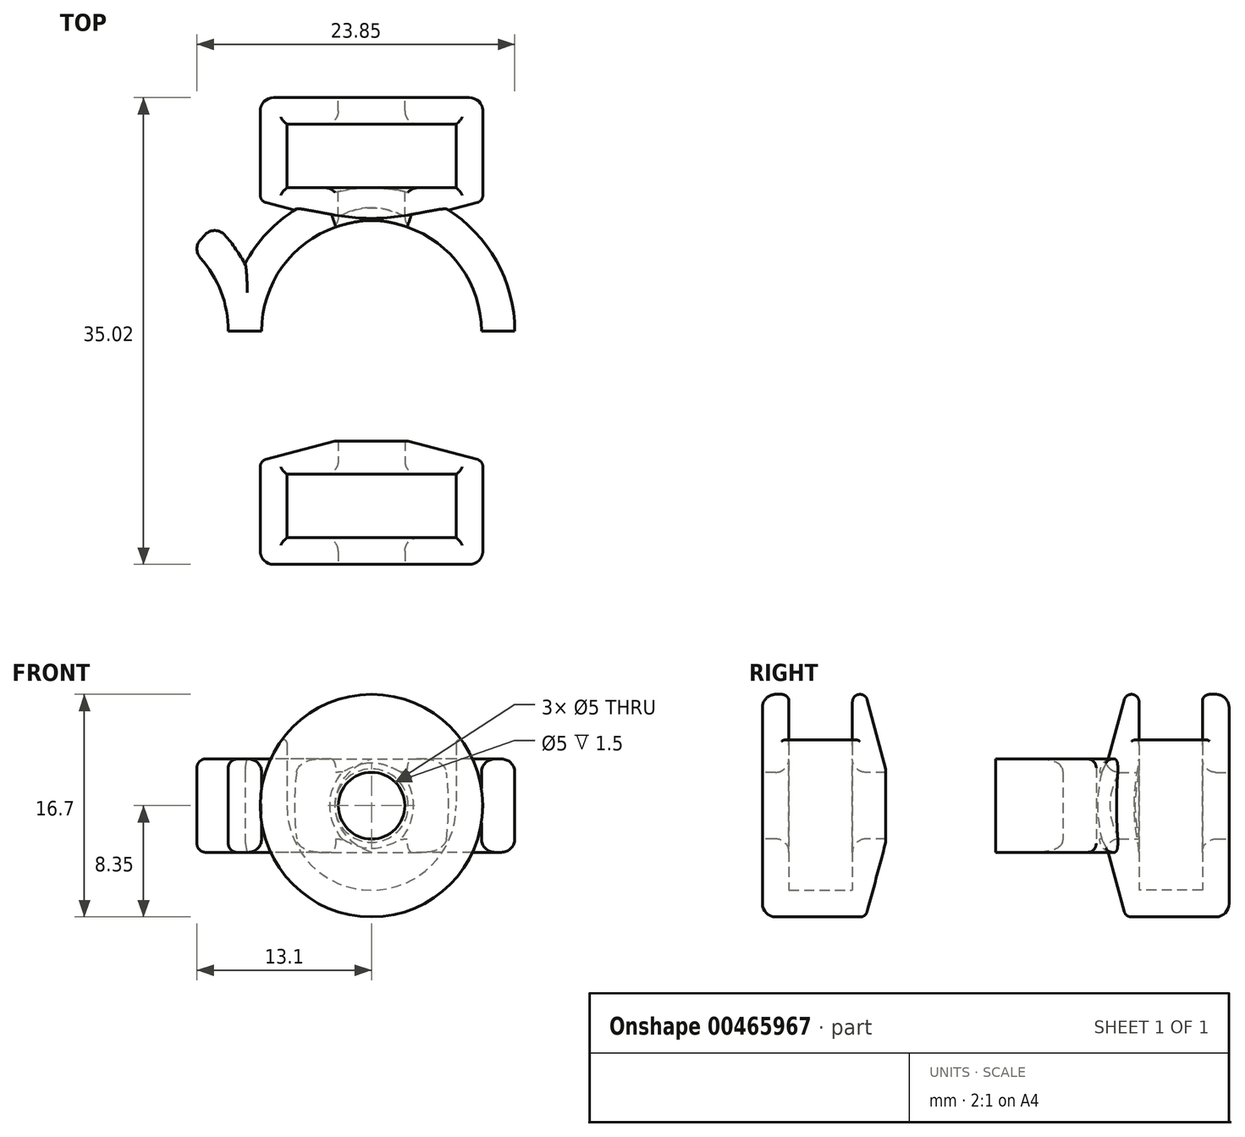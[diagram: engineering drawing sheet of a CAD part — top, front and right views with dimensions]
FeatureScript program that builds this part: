
annotation { "Feature Type Name" : "Feature", "Feature Type Description" : "" }
export const myFeature = defineFeature(function(context is Context, id is Id, definition is map)
    precondition{}
    {
        {
            var Q0;
            Q0=qCreatedBy(makeId("Top.planeOp"),FACE);
            var sketch = newSketch(context, id + "F0", { "sketchPlane" : qUnion([Q0])});
            skCircle(sketch, "E0", {"center": v(0, 0) * mm, "radius": 8.25 * mm});
            skCircle(sketch, "E1", {"center": v(0, 0) * mm, "radius": 10.75 * mm});
            skSolve(sketch);
        }
        {
            var Q0;
            Q0=qCreatedBy(makeId("Top.planeOp"),FACE);
            var sketch = newSketch(context, id + "F1", { "sketchPlane" : qUnion([Q0])});
            skLineSegment(sketch, "E2", {"start": v(0, 0) * mm, "end": v(0, 8.25) * mm, "construction": true});
            skLineSegment(sketch, "E3", {"start": v(0, 8.25) * mm, "end": v(8.35, 8.25) * mm});
            skLineSegment(sketch, "E4", {"start": v(8.35, 8.25) * mm, "end": v(8.35, 17.51) * mm});
            skLineSegment(sketch, "E5", {"start": v(8.35, 17.51) * mm, "end": v(0, 17.51) * mm});
            skLineSegment(sketch, "E6", {"start": v(0, 17.51) * mm, "end": v(0, 15.51) * mm});
            skLineSegment(sketch, "E7", {"start": v(0, 15.51) * mm, "end": v(6.35, 15.51) * mm});
            skLineSegment(sketch, "E8", {"start": v(6.35, 15.51) * mm, "end": v(6.35, 10.75) * mm});
            skLineSegment(sketch, "E9", {"start": v(0, 8.25) * mm, "end": v(0, 10.75) * mm});
            skLineSegment(sketch, "E10", {"start": v(0, 10.75) * mm, "end": v(6.35, 10.75) * mm});
            skLineSegment(sketch, "E11", {"start": v(0, 15.51) * mm, "end": v(0, 10.75) * mm, "construction": true});
            skSolve(sketch);
        }
        {
            var Q0;
            Q0 = qSketchRegion(id + "F1", true);
            var Q1;
            Q1=sQuery(id+"F1.wireOp",EDGE,"E2");
            revolve(context, id + "F2", {"surfaceOperationType" : NewSurfaceOperationType.NEW, "entities" : qUnion([Q0]), "axis" : qUnion([Q1]), "revolveType" : RevolveType.FULL});
        }
        {
            var Q0;
            Q0 = qSketchRegion(id + "F0", true);
            extrude(context, id + "F3", {"entities" : qUnion([Q0]), "endBound" : BoundingType.SYMMETRIC, "depth" : 7 * mm, "offsetDistance" : 25 * mm});
        }
        {
            var Q0;
            Q0=qCreatedBy(makeId("Top.planeOp"),FACE);
            var sketch = newSketch(context, id + "F4", { "sketchPlane" : qUnion([Q0])});
            skLineSegment(sketch, "E12", {"start": v(6.35, 10.75) * mm, "end": v(6.35, 15.51) * mm});
            skLineSegment(sketch, "E13", {"start": v(6.35, 15.51) * mm, "end": v(-6.35, 15.51) * mm});
            skLineSegment(sketch, "E14", {"start": v(-6.35, 15.51) * mm, "end": v(-6.35, 10.75) * mm});
            skLineSegment(sketch, "E15", {"start": v(0, 10.75) * mm, "end": v(-6.35, 10.75) * mm});
            skLineSegment(sketch, "E16", {"start": v(0, 10.75) * mm, "end": v(6.35, 10.75) * mm});
            skLineSegment(sketch, "E17", {"start": v(0, 0) * mm, "end": v(0, 8.25) * mm, "construction": true});
            skLineSegment(sketch, "E18", {"start": v(0, 8.25) * mm, "end": v(0, 10.75) * mm, "construction": true});
            skSolve(sketch);
        }
        {
            var Q0;
            Q0 = qSketchRegion(id + "F4", true);
            extrude(context, id + "F5", {"entities" : qUnion([Q0]), "operationType" : NewBodyOperationType.REMOVE, "depth" : 9.6 * mm, "offsetDistance" : 25 * mm});
        }
        {
            var Q0;
            Q0=makeQuery(id+"F2.opRevolve","SWEPT_FACE",FACE,{"disambiguationData":[OSD([sQuery(id+"F1.wireOp",EDGE,"E5")])]});
            var sketch = newSketch(context, id + "F6", { "sketchPlane" : qUnion([Q0])});
            skCircle(sketch, "E19", {"center": v(0, 0) * mm, "radius": 2.5 * mm});
            skSolve(sketch);
        }
        {
            var Q0;
            Q0 = qSketchRegion(id + "F6", true);
            extrude(context, id + "F7", {"entities" : qUnion([Q0]), "operationType" : NewBodyOperationType.REMOVE, "oppositeDirection" : true, "depth" : 19.1 * mm, "offsetDistance" : 25 * mm});
        }
        {
            var Q0;
            Q0=makeQuery(id+"F2.opRevolve","SWEPT_EDGE",EDGE,{"disambiguationData":[OSD([sQuery(id+"F1.wireOp",EDGE,"E3"),sQuery(id+"F1.wireOp",EDGE,"E4")])]});
            chamfer(context, id + "F8", {"entities" : qUnion([Q0]), "chamferType" : ChamferType.OFFSET_ANGLE, "width" : 1.5 * mm, "oppositeDirection" : true, "angle" : 75 * degree, "tangentPropagation" : true});
        }
        {
            var Q0;
            Q0=makeQuery(id+"F5.boolean.opBoolean","INTERSECT",EDGE,{"derivedFrom":[makeQuery(id+"F2.opRevolve","SWEPT_FACE",FACE,{"disambiguationData":[OSD([sQuery(id+"F1.wireOp",EDGE,"E4")])]}),makeQuery(id+"F5.opExtrude","SWEPT_FACE",FACE,{"disambiguationData":[OSD([sQuery(id+"F4.wireOp",EDGE,"E14")])]})]});
            var Q1;
            Q1=makeQuery(id+"F5.boolean.opBoolean","INTERSECT",EDGE,{"derivedFrom":[makeQuery(id+"F2.opRevolve","SWEPT_FACE",FACE,{"disambiguationData":[OSD([sQuery(id+"F1.wireOp",EDGE,"E4")])]}),makeQuery(id+"F5.opExtrude","SWEPT_FACE",FACE,{"disambiguationData":[OSD([sQuery(id+"F4.wireOp",EDGE,"E12")])]})]});
            fillet(context, id + "F9", {"entities" : qUnion([Q0, Q1]), "radius" : .25 * mm, "tangentPropagation" : true, "allowEdgeOverflow" : false});
        }
        {
            var Q0;
            {var subQ0=sQuery(id+"F1.wireOp",EDGE,"E4");Q0=makeQuery(id+"F8.opChamfer","BLEND_EDGE",EDGE,{"blendedFrom":[makeQuery(id+"F2.opRevolve","SWEPT_EDGE",EDGE,{"disambiguationData":[OSD([sQuery(id+"F1.wireOp",EDGE,"E3"),subQ0])]}),makeQuery(id+"F2.opRevolve","SWEPT_FACE",FACE,{"disambiguationData":[OSD([subQ0])]})],"blendedInto":[makeQuery(id+"F2.opRevolve","SWEPT_FACE",FACE,{"disambiguationData":[OSD([subQ0])]})]});}
            var Q1;
            Q1=makeQuery(id+"F5.boolean.opBoolean","INTERSECT",EDGE,{"derivedFrom":[makeQuery(id+"F2.opRevolve","SWEPT_FACE",FACE,{"disambiguationData":[OSD([sQuery(id+"F1.wireOp",EDGE,"E4")])]}),makeQuery(id+"F5.opExtrude","SWEPT_FACE",FACE,{"disambiguationData":[OSD([sQuery(id+"F4.wireOp",EDGE,"E15"),sQuery(id+"F4.wireOp",EDGE,"E16")])]})]});
            var Q2;
            Q2=makeQuery(id+"F5.boolean.opBoolean","INTERSECT",EDGE,{"derivedFrom":[makeQuery(id+"F2.opRevolve","SWEPT_FACE",FACE,{"disambiguationData":[OSD([sQuery(id+"F1.wireOp",EDGE,"E4")])]}),makeQuery(id+"F5.opExtrude","SWEPT_FACE",FACE,{"disambiguationData":[OSD([sQuery(id+"F4.wireOp",EDGE,"E13")])]})]});
            fillet(context, id + "F10", {"entities" : qUnion([Q0, Q1, Q2]), "radius" : .55 * mm, "tangentPropagation" : true, "allowEdgeOverflow" : false});
        }
        {
            var Q0;
            Q0=makeQuery(id+"F2.opRevolve","SWEPT_EDGE",EDGE,{"disambiguationData":[OSD([sQuery(id+"F1.wireOp",EDGE,"E4"),sQuery(id+"F1.wireOp",EDGE,"E5")])]});
            var Q1;
            Q1=makeQuery(id+"F7.boolean.opBoolean","COPY",EDGE,{"derivedFrom":makeQuery(id+"F7.opExtrude","CAP_EDGE",EDGE,{"disambiguationData":[OSD([sQuery(id+"F6.wireOp",EDGE,"E19")])],"isStart":true})});
            var Q2;
            Q2=makeQuery(id+"F7.boolean.opBoolean","INTERSECT",EDGE,{"derivedFrom":[makeQuery(id+"F5.boolean.opBoolean","MERGE",FACE,{"derivedFrom":[makeQuery(id+"F2.opRevolve","SWEPT_FACE",FACE,{"disambiguationData":[OSD([sQuery(id+"F1.wireOp",EDGE,"E10")])]}),makeQuery(id+"F5.opExtrude","SWEPT_FACE",FACE,{"disambiguationData":[OSD([sQuery(id+"F4.wireOp",EDGE,"E15"),sQuery(id+"F4.wireOp",EDGE,"E16")])]})]}),makeQuery(id+"F7.opExtrude","SWEPT_FACE",FACE,{"disambiguationData":[OSD([sQuery(id+"F6.wireOp",EDGE,"E19")])]})]});
            var Q3;
            Q3=makeQuery(id+"F7.boolean.opBoolean","INTERSECT",EDGE,{"derivedFrom":[makeQuery(id+"F5.boolean.opBoolean","MERGE",FACE,{"derivedFrom":[makeQuery(id+"F2.opRevolve","SWEPT_FACE",FACE,{"disambiguationData":[OSD([sQuery(id+"F1.wireOp",EDGE,"E7")])]}),makeQuery(id+"F5.opExtrude","SWEPT_FACE",FACE,{"disambiguationData":[OSD([sQuery(id+"F4.wireOp",EDGE,"E13")])]})]}),makeQuery(id+"F7.opExtrude","SWEPT_FACE",FACE,{"disambiguationData":[OSD([sQuery(id+"F6.wireOp",EDGE,"E19")])]})]});
            fillet(context, id + "F11", {"entities" : qUnion([Q0, Q1, Q2, Q3]), "radius" : 1 * mm, "tangentPropagation" : true, "allowEdgeOverflow" : false});
        }
        {
            var Q0;
            Q0=qCreatedBy(makeId("Top.planeOp"),FACE);
            var sketch = newSketch(context, id + "F12", { "sketchPlane" : qUnion([Q0])});
            skCircle(sketch, "E20", {"center": v(0, 0) * mm, "radius": 8.25 * mm, "construction": true});
            skCircle(sketch, "E21", {"center": v(0, 0) * mm, "radius": 10.75 * mm, "construction": true});
            skLineSegment(sketch, "E22", {"start": v(0, 0) * mm, "end": v(-5.52, 6.13) * mm, "construction": true});
            skLineSegment(sketch, "E23", {"start": v(-5.52, 6.13) * mm, "end": v(-7.2, 7.99) * mm, "construction": true});
            skLineSegment(sketch, "E24", {"start": v(0, 0) * mm, "end": v(-8.25, 0) * mm, "construction": true});
            skLineSegment(sketch, "E25", {"start": v(-8.25, 0) * mm, "end": v(-10.75, 0) * mm, "construction": true});
            skArc(sketch, "E26", {"start": v(-8.25, 0) * mm, "mid": v(-7.54, 3.36) * mm, "end": v(-5.52, 6.13) * mm});
            skArc(sketch, "E27", {"start": v(-10.75, 0) * mm, "mid": v(-9.82, 4.37) * mm, "end": v(-7.2, 7.99) * mm});
            skLineSegment(sketch, "E28", {"start": v(-7.2, 7.99) * mm, "end": v(-5.52, 6.13) * mm});
            skLineSegment(sketch, "E29", {"start": v(-8.25, 0) * mm, "end": v(-10.75, 0) * mm});
            skLineSegment(sketch, "E30", {"start": v(-9.5, 0) * mm, "end": v(-9.5, 7.58) * mm, "construction": true});
            skArc(sketch, "E31.MirrorCS", {"start": v(-8.25, 0) * mm, "mid": v(-9.18, 4.37) * mm, "end": v(-11.8, 7.99) * mm});
            skLineSegment(sketch, "E32.MirrorCS", {"start": v(-11.8, 7.99) * mm, "end": v(-13.48, 6.13) * mm});
            skArc(sketch, "E33.MirrorCS", {"start": v(-10.75, 0) * mm, "mid": v(-11.46, 3.36) * mm, "end": v(-13.48, 6.13) * mm});
            skLineSegment(sketch, "E34.MirrorCS", {"start": v(-10.75, 0) * mm, "end": v(-8.25, 0) * mm});
            skSolve(sketch);
        }
        {
            var Q0;
            {var subQ1=sQuery(id+"F12.wireOp",EDGE,"E32.MirrorCS");Q0=makeQuery(id+"F12.imprint","IMPRINT",FACE,{"disambiguationData":[TD([[makeQuery(id+"F12.imprint","IMPRINT",EDGE,{"derivedFrom":subQ1}),1.0]])]});}
            extrude(context, id + "F13", {"entities" : qUnion([Q0]), "operationType" : NewBodyOperationType.ADD, "endBound" : BoundingType.SYMMETRIC, "depth" : 7 * mm, "offsetDistance" : 25 * mm});
        }
        {
            var Q0;
            Q0=qCreatedBy(makeId("Top.planeOp"),FACE);
            var sketch = newSketch(context, id + "F14", { "sketchPlane" : qUnion([Q0])});
            skLineSegment(sketch, "E35.bottom", {"start": v(-12.57, 0) * mm, "end": v(12.8, 0) * mm});
            skLineSegment(sketch, "E35.top", {"start": v(-12.57, -11.24) * mm, "end": v(12.8, -11.24) * mm});
            skLineSegment(sketch, "E35.left", {"start": v(-12.57, 0) * mm, "end": v(-12.57, -11.24) * mm});
            skLineSegment(sketch, "E35.right", {"start": v(12.8, 0) * mm, "end": v(12.8, -11.24) * mm});
            skSolve(sketch);
        }
        {
            var Q0;
            Q0 = qSketchRegion(id + "F14", true);
            extrude(context, id + "F15", {"entities" : qUnion([Q0]), "operationType" : NewBodyOperationType.REMOVE, "endBound" : BoundingType.SYMMETRIC, "oppositeDirection" : true, "depth" : 25 * mm, "offsetDistance" : 25 * mm});
        }
        {
            var Q0;
            Q0=makeQuery(id+"F2.opRevolve","SWEPT_BODY",BODY,{"disambiguationData":[OSD([sQuery(id+"F1.wireOp",EDGE,"E3"),sQuery(id+"F1.wireOp",EDGE,"E4"),sQuery(id+"F1.wireOp",EDGE,"E5"),sQuery(id+"F1.wireOp",EDGE,"E6"),sQuery(id+"F1.wireOp",EDGE,"E7"),sQuery(id+"F1.wireOp",EDGE,"E8"),sQuery(id+"F1.wireOp",EDGE,"E9"),sQuery(id+"F1.wireOp",EDGE,"E10")])]});
            var Q1;
            Q1=qCreatedBy(makeId("Front.planeOp"),FACE);
            mirror(context, id + "F16", {"operationType" : NewBodyOperationType.ADD, "entities" : qUnion([Q0]), "mirrorPlane" : qUnion([Q1])});
        }
        {
            var Q0;
            {var subQ0=makeQuery(id+"F3.opExtrude","CAP_EDGE",EDGE,{"disambiguationData":[OSD([sQuery(id+"F0.wireOp",EDGE,"E0")])],"isStart":false});Q0=makeQuery(id+"F16.boolean.opBoolean","MERGE",EDGE,{"derivedFrom":[subQ0,makeQuery(id+"F16.opPattern","COPY",EDGE,{"derivedFrom":subQ0,"instanceName":"1"})]});}
            var Q1;
            Q1=makeQuery(id+"F16.opPattern","COPY",EDGE,{"derivedFrom":makeQuery(id+"F7.boolean.opBoolean","INTERSECT",EDGE,{"derivedFrom":[makeQuery(id+"F3.opExtrude","SWEPT_FACE",FACE,{"disambiguationData":[OSD([sQuery(id+"F0.wireOp",EDGE,"E0")])]}),makeQuery(id+"F7.opExtrude","SWEPT_FACE",FACE,{"disambiguationData":[OSD([sQuery(id+"F6.wireOp",EDGE,"E19")])]})]}),"instanceName":"1"});
            var Q2;
            {var subQ0=makeQuery(id+"F3.opExtrude","CAP_EDGE",EDGE,{"disambiguationData":[OSD([sQuery(id+"F0.wireOp",EDGE,"E0")])],"isStart":true});Q2=makeQuery(id+"F16.boolean.opBoolean","MERGE",EDGE,{"derivedFrom":[subQ0,makeQuery(id+"F16.opPattern","COPY",EDGE,{"derivedFrom":subQ0,"instanceName":"1"})]});}
            var Q3;
            Q3=makeQuery(id+"F7.boolean.opBoolean","INTERSECT",EDGE,{"derivedFrom":[makeQuery(id+"F3.opExtrude","SWEPT_FACE",FACE,{"disambiguationData":[OSD([sQuery(id+"F0.wireOp",EDGE,"E0")])]}),makeQuery(id+"F7.opExtrude","SWEPT_FACE",FACE,{"disambiguationData":[OSD([sQuery(id+"F6.wireOp",EDGE,"E19")])]})]});
            fillet(context, id + "F17", {"entities" : qUnion([Q0, Q1, Q2, Q3]), "radius" : 1 * mm, "tangentPropagation" : true, "allowEdgeOverflow" : false});
        }
        {
            var Q0;
            {var subQ0=sQuery(id+"F12.wireOp",EDGE,"E34.MirrorCS");var subQ1=sQuery(id+"F0.wireOp",EDGE,"E1");var subQ2=makeQuery(id+"F13.boolean.opBoolean","SPLIT",EDGE,{"disambiguationData":[TD([makeQuery(id+"F13.opExtrude","SWEPT_FACE",FACE,{"disambiguationData":[OSD([subQ0])]})])],"derivedFrom":makeQuery(id+"F3.opExtrude","CAP_EDGE",EDGE,{"disambiguationData":[OSD([subQ1])],"isStart":true})});Q0=makeQuery(id+"F16.boolean.opBoolean","MERGE",EDGE,{"derivedFrom":[subQ2,makeQuery(id+"F16.opPattern","COPY",EDGE,{"derivedFrom":subQ2,"instanceName":"1"})]});}
            var Q1;
            {var subQ0=sQuery(id+"F0.wireOp",EDGE,"E1");var subQ1=sQuery(id+"F12.wireOp",EDGE,"E34.MirrorCS");var subQ2=makeQuery(id+"F13.boolean.opBoolean","SPLIT",EDGE,{"disambiguationData":[TD([makeQuery(id+"F13.opExtrude","SWEPT_FACE",FACE,{"disambiguationData":[OSD([subQ1])]})])],"derivedFrom":makeQuery(id+"F3.opExtrude","CAP_EDGE",EDGE,{"disambiguationData":[OSD([subQ0])],"isStart":false})});Q1=makeQuery(id+"F16.boolean.opBoolean","MERGE",EDGE,{"derivedFrom":[subQ2,makeQuery(id+"F16.opPattern","COPY",EDGE,{"derivedFrom":subQ2,"instanceName":"1"})]});}
            var Q2;
            {var subQ0=sQuery(id+"F0.wireOp",EDGE,"E1");var subQ1=sQuery(id+"F12.wireOp",EDGE,"E31.MirrorCS");Q2=makeQuery(id+"F13.boolean.opBoolean","SPLIT",EDGE,{"disambiguationData":[TD([makeQuery(id+"F13.opExtrude","SWEPT_FACE",FACE,{"disambiguationData":[OSD([subQ1])]})])],"derivedFrom":makeQuery(id+"F3.opExtrude","CAP_EDGE",EDGE,{"disambiguationData":[OSD([subQ0])],"isStart":false})});}
            var Q3;
            {var subQ0=sQuery(id+"F0.wireOp",EDGE,"E1");var subQ1=sQuery(id+"F12.wireOp",EDGE,"E31.MirrorCS");Q3=makeQuery(id+"F16.opPattern","COPY",EDGE,{"derivedFrom":makeQuery(id+"F13.boolean.opBoolean","SPLIT",EDGE,{"disambiguationData":[TD([makeQuery(id+"F13.opExtrude","SWEPT_FACE",FACE,{"disambiguationData":[OSD([subQ1])]})])],"derivedFrom":makeQuery(id+"F3.opExtrude","CAP_EDGE",EDGE,{"disambiguationData":[OSD([subQ0])],"isStart":false})}),"instanceName":"1"});}
            var Q4;
            {var subQ0=sQuery(id+"F12.wireOp",EDGE,"E31.MirrorCS");var subQ1=sQuery(id+"F0.wireOp",EDGE,"E1");Q4=makeQuery(id+"F13.boolean.opBoolean","SPLIT",EDGE,{"disambiguationData":[TD([makeQuery(id+"F13.opExtrude","SWEPT_FACE",FACE,{"disambiguationData":[OSD([subQ0])]})])],"derivedFrom":makeQuery(id+"F3.opExtrude","CAP_EDGE",EDGE,{"disambiguationData":[OSD([subQ1])],"isStart":true})});}
            var Q5;
            {var subQ0=sQuery(id+"F12.wireOp",EDGE,"E31.MirrorCS");var subQ1=sQuery(id+"F0.wireOp",EDGE,"E1");Q5=makeQuery(id+"F16.opPattern","COPY",EDGE,{"derivedFrom":makeQuery(id+"F13.boolean.opBoolean","SPLIT",EDGE,{"disambiguationData":[TD([makeQuery(id+"F13.opExtrude","SWEPT_FACE",FACE,{"disambiguationData":[OSD([subQ0])]})])],"derivedFrom":makeQuery(id+"F3.opExtrude","CAP_EDGE",EDGE,{"disambiguationData":[OSD([subQ1])],"isStart":true})}),"instanceName":"1"});}
            var Q6;
            {var subQ0=sQuery(id+"F0.wireOp",EDGE,"E1");var subQ1=sQuery(id+"F12.wireOp",EDGE,"E33.MirrorCS");var subQ2=makeQuery(id+"F13.boolean.opBoolean","SPLIT",EDGE,{"disambiguationData":[TD([makeQuery(id+"F13.opExtrude","SWEPT_FACE",FACE,{"disambiguationData":[OSD([subQ1])]})])],"derivedFrom":makeQuery(id+"F3.opExtrude","CAP_EDGE",EDGE,{"disambiguationData":[OSD([subQ0])],"isStart":false})});Q6=makeQuery(id+"F16.boolean.opBoolean","MERGE",EDGE,{"derivedFrom":[subQ2,makeQuery(id+"F16.opPattern","COPY",EDGE,{"derivedFrom":subQ2,"instanceName":"1"})]});}
            var Q7;
            {var subQ0=sQuery(id+"F12.wireOp",EDGE,"E33.MirrorCS");var subQ1=sQuery(id+"F0.wireOp",EDGE,"E1");var subQ2=makeQuery(id+"F13.boolean.opBoolean","SPLIT",EDGE,{"disambiguationData":[TD([makeQuery(id+"F13.opExtrude","SWEPT_FACE",FACE,{"disambiguationData":[OSD([subQ0])]})])],"derivedFrom":makeQuery(id+"F3.opExtrude","CAP_EDGE",EDGE,{"disambiguationData":[OSD([subQ1])],"isStart":true})});Q7=makeQuery(id+"F16.boolean.opBoolean","MERGE",EDGE,{"derivedFrom":[subQ2,makeQuery(id+"F16.opPattern","COPY",EDGE,{"derivedFrom":subQ2,"instanceName":"1"})]});}
            fillet(context, id + "F18", {"entities" : qUnion([Q0, Q1, Q2, Q3, Q4, Q5, Q6, Q7]), "radius" : 1 * mm, "tangentPropagation" : true, "allowEdgeOverflow" : false});
        }
        {
            var Q0;
            Q0=makeQuery(id+"F13.opExtrude","SWEPT_EDGE",EDGE,{"disambiguationData":[OSD([sQuery(id+"F12.wireOp",EDGE,"E31.MirrorCS"),sQuery(id+"F12.wireOp",EDGE,"E32.MirrorCS")])]});
            var Q1;
            Q1=makeQuery(id+"F13.opExtrude","SWEPT_EDGE",EDGE,{"disambiguationData":[OSD([sQuery(id+"F12.wireOp",EDGE,"E32.MirrorCS"),sQuery(id+"F12.wireOp",EDGE,"E33.MirrorCS")])]});
            var Q2;
            Q2=makeQuery(id+"F16.opPattern","COPY",EDGE,{"derivedFrom":makeQuery(id+"F13.opExtrude","SWEPT_EDGE",EDGE,{"disambiguationData":[OSD([sQuery(id+"F12.wireOp",EDGE,"E32.MirrorCS"),sQuery(id+"F12.wireOp",EDGE,"E33.MirrorCS")])]}),"instanceName":"1"});
            var Q3;
            Q3=makeQuery(id+"F16.opPattern","COPY",EDGE,{"derivedFrom":makeQuery(id+"F13.opExtrude","SWEPT_EDGE",EDGE,{"disambiguationData":[OSD([sQuery(id+"F12.wireOp",EDGE,"E31.MirrorCS"),sQuery(id+"F12.wireOp",EDGE,"E32.MirrorCS")])]}),"instanceName":"1"});
            fillet(context, id + "F19", {"entities" : qUnion([Q0, Q1, Q2, Q3]), "radius" : 1 * mm, "tangentPropagation" : true, "allowEdgeOverflow" : false});
        }
        {
            var Q0;
            {var subQ0=makeQuery(id+"F13.opExtrude","CAP_EDGE",EDGE,{"disambiguationData":[OSD([sQuery(id+"F12.wireOp",EDGE,"E33.MirrorCS")])],"isStart":false});Q0=makeQuery(id+"F16.boolean.opBoolean","MERGE",EDGE,{"derivedFrom":[subQ0,makeQuery(id+"F16.opPattern","COPY",EDGE,{"derivedFrom":subQ0,"instanceName":"1"})]});}
            var Q1;
            {var subQ0=makeQuery(id+"F13.opExtrude","CAP_EDGE",EDGE,{"disambiguationData":[OSD([sQuery(id+"F12.wireOp",EDGE,"E33.MirrorCS")])],"isStart":true});Q1=makeQuery(id+"F16.boolean.opBoolean","MERGE",EDGE,{"derivedFrom":[subQ0,makeQuery(id+"F16.opPattern","COPY",EDGE,{"derivedFrom":subQ0,"instanceName":"1"})]});}
            fillet(context, id + "F20", {"entities" : qUnion([Q0, Q1]), "radius" : .65 * mm, "tangentPropagation" : true, "allowEdgeOverflow" : false});
        }
    });
